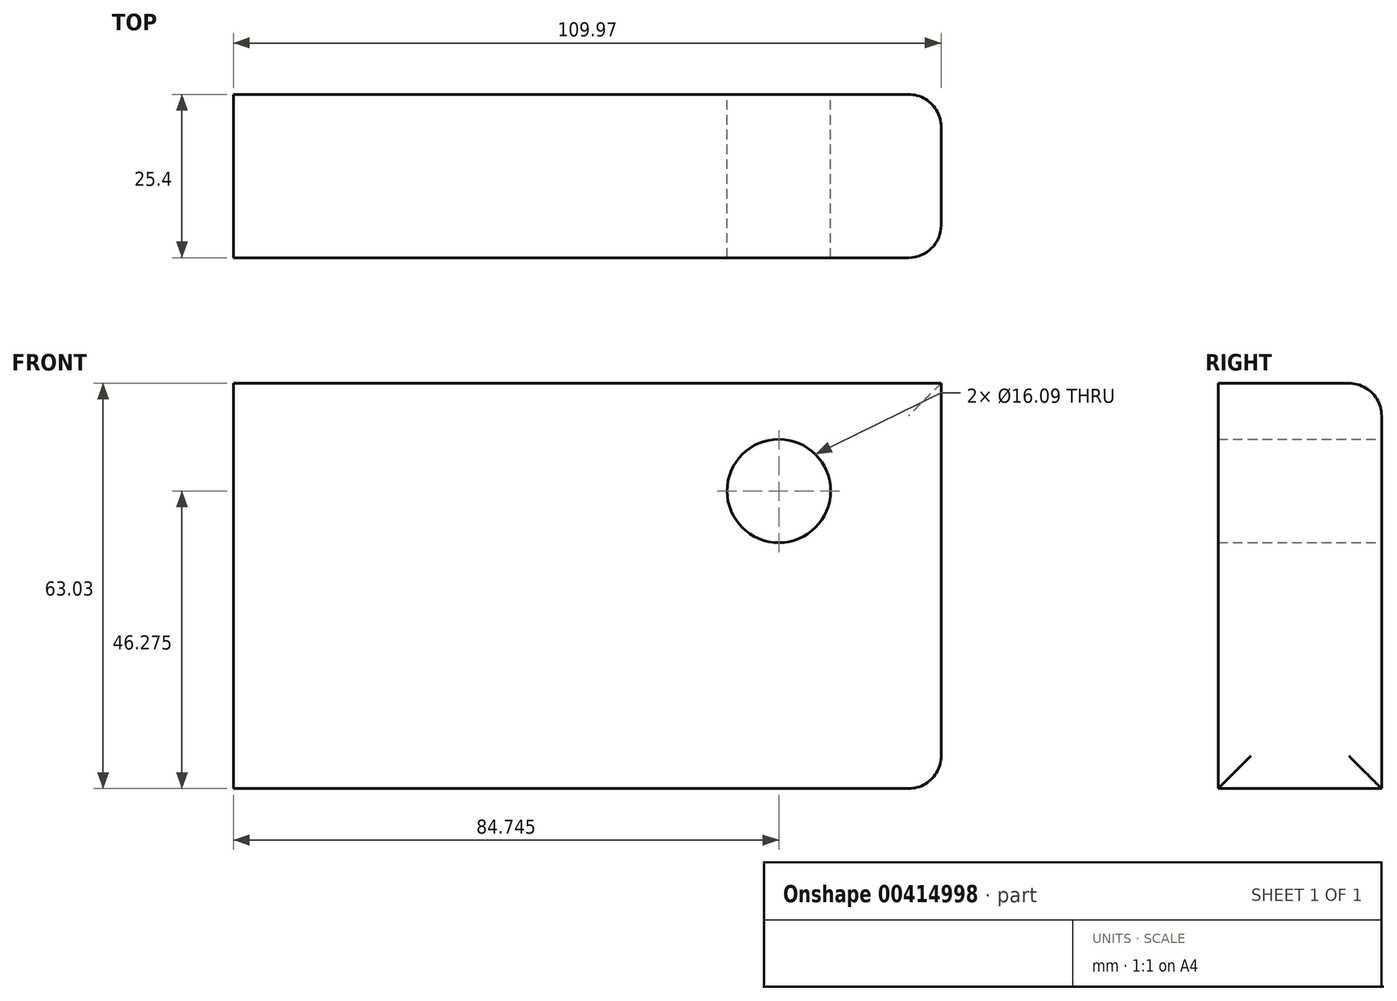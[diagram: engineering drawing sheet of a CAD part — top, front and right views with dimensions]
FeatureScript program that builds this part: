
annotation { "Feature Type Name" : "Feature", "Feature Type Description" : "" }
export const myFeature = defineFeature(function(context is Context, id is Id, definition is map)
    precondition{}
    {
        {
            var Q0;
            Q0=qCreatedBy(makeId("Front.planeOp"),FACE);
            var sketch = newSketch(context, id + "F0", { "sketchPlane" : qUnion([Q0])});
            skLineSegment(sketch, "E0.bottom", {"start": v(-62.68, 36.26) * mm, "end": v(47.3, 36.26) * mm});
            skLineSegment(sketch, "E0.top", {"start": v(-62.68, -26.77) * mm, "end": v(47.3, -26.77) * mm});
            skLineSegment(sketch, "E0.left", {"start": v(-62.68, 36.26) * mm, "end": v(-62.68, -26.77) * mm});
            skLineSegment(sketch, "E0.right", {"start": v(47.3, 36.26) * mm, "end": v(47.3, -26.77) * mm});
            skLineSegment(sketch, "E1.bottom", {"start": v(-62.68, 36.26) * mm, "end": v(0, 36.26) * mm});
            skLineSegment(sketch, "E1.top", {"start": v(-62.68, 49.87) * mm, "end": v(0, 49.87) * mm});
            skLineSegment(sketch, "E1.left", {"start": v(-62.68, 36.26) * mm, "end": v(-62.68, 49.87) * mm});
            skLineSegment(sketch, "E1.right", {"start": v(0, 36.26) * mm, "end": v(0, 49.87) * mm});
            skCircle(sketch, "E2", {"center": v(22.06, 19.5) * mm, "radius": 8.04 * mm});
            skSolve(sketch);
        }
        {
            var Q0;
            Q0=makeQuery(id+"F0.imprint","IMPRINT",FACE,{"disambiguationData":[TD([[makeQuery(id+"F0.imprint","IMPRINT",EDGE,{"derivedFrom":sQuery(id+"F0.wireOp",EDGE,"E0.bottom")}),-1.0]])]});
            extrude(context, id + "F1", {"entities" : qUnion([Q0]), "depth" : 25.4 * mm, "offsetDistance" : 25.4 * mm});
        }
        {
            var Q0;
            Q0=makeQuery(id+"F1.opExtrude","CAP_EDGE",EDGE,{"disambiguationData":[OSD([sQuery(id+"F0.wireOp",EDGE,"E0.bottom"),sQuery(id+"F0.wireOp",EDGE,"E1.bottom")])],"isStart":true});
            var Q1;
            Q1=makeQuery(id+"F1.opExtrude","CAP_EDGE",EDGE,{"disambiguationData":[OSD([sQuery(id+"F0.wireOp",EDGE,"E0.right")])],"isStart":true});
            var Q2;
            Q2=makeQuery(id+"F1.opExtrude","SWEPT_EDGE",EDGE,{"disambiguationData":[OSD([sQuery(id+"F0.wireOp",EDGE,"E0.top"),sQuery(id+"F0.wireOp",EDGE,"E0.right")])]});
            var Q3;
            Q3=makeQuery(id+"F1.opExtrude","CAP_EDGE",EDGE,{"disambiguationData":[OSD([sQuery(id+"F0.wireOp",EDGE,"E0.right")])],"isStart":false});
            fillet(context, id + "F2", {"entities" : qUnion([Q0, Q1, Q2, Q3]), "radius" : 5.08 * mm, "tangentPropagation" : true, "allowEdgeOverflow" : false});
        }
    });
